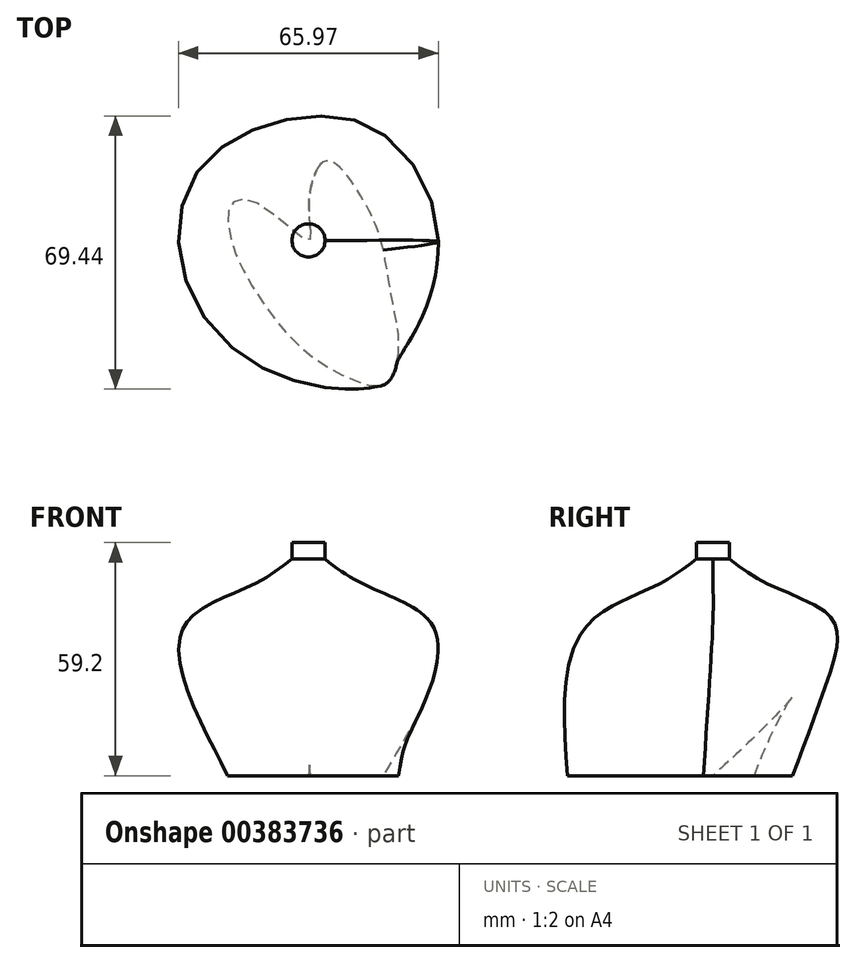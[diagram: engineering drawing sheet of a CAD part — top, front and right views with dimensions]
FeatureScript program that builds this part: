
annotation { "Feature Type Name" : "Feature", "Feature Type Description" : "" }
export const myFeature = defineFeature(function(context is Context, id is Id, definition is map)
    precondition{}
    {
        {
            var Q0;
            Q0=qCreatedBy(makeId("Top.planeOp"),FACE);
            var sketch = newSketch(context, id + "F0", { "sketchPlane" : qUnion([Q0])});
            skFitSpline(sketch, "E0", {"points": [v(0, 0) * mm, v(-12.97, 9.4) * mm, v(-19.64, 9.13) * mm, v(-19.62, 0) * mm, v(-12.36, -14.68) * mm, v(0, -28.81) * mm, v(12.9, -36.01) * mm, v(19.87, -36.29) * mm, v(22.92, -26.63) * mm, v(21.05, -14.06) * mm, v(18.37, 0) * mm, v(12.48, 12.6) * mm, v(4.5, 20.2) * mm, v(0, 8.91) * mm, v(0, 0) * mm]});
            skSolve(sketch);
        }
        {
            var Q0;
            Q0=qCreatedBy(makeId("Top.planeOp"),FACE);
            cPlane(context, id + "F1", {"entities" : qUnion([Q0]), "cplaneType" : CPlaneType.OFFSET, "offset" : 40 * mm, "width" : 152.4 * mm, "height" : 152.4 * mm});
        }
        {
            var Q0;
            Q0=qCreatedBy(id+"F1.planeOp",FACE);
            var sketch = newSketch(context, id + "F2", { "sketchPlane" : qUnion([Q0])});
            skCircle(sketch, "E1", {"center": v(0, 0) * mm, "radius": 30.1 * mm});
            skSolve(sketch);
        }
        {
            var Q0;
            Q0=qCreatedBy(makeId("Top.planeOp"),FACE);
            cPlane(context, id + "F3", {"entities" : qUnion([Q0]), "cplaneType" : CPlaneType.OFFSET, "offset" : 50 * mm, "width" : 150 * mm, "height" : 150 * mm});
        }
        {
            var Q0;
            Q0=qCreatedBy(id+"F3.planeOp",FACE);
            var sketch = newSketch(context, id + "F4", { "sketchPlane" : qUnion([Q0])});
            skCircle(sketch, "E2", {"center": v(0, 0) * mm, "radius": 11.38 * mm});
            skSolve(sketch);
        }
        {
            var Q0;
            Q0=qCreatedBy(makeId("Top.planeOp"),FACE);
            cPlane(context, id + "F5", {"entities" : qUnion([Q0]), "cplaneType" : CPlaneType.OFFSET, "offset" : 55 * mm, "width" : 150 * mm, "height" : 150 * mm});
        }
        {
            var Q0;
            Q0=qCreatedBy(id+"F5.planeOp",FACE);
            var sketch = newSketch(context, id + "F6", { "sketchPlane" : qUnion([Q0])});
            skCircle(sketch, "E3", {"center": v(0, 0) * mm, "radius": 4.2 * mm});
            skSolve(sketch);
        }
        {
            var Q0;
            Q0 = qSketchRegion(id + "F6", true);
            var Q1;
            Q1 = qSketchRegion(id + "F4", true);
            var Q2;
            Q2 = qSketchRegion(id + "F2", true);
            var Q3;
            Q3 = qSketchRegion(id + "F0", true);
            loft(context, id + "F7", {"sheetProfilesArray" : [{ "sheetProfileEntities" : qUnion([Q0]) }, { "sheetProfileEntities" : qUnion([Q1]) }, { "sheetProfileEntities" : qUnion([Q2]) }, { "sheetProfileEntities" : qUnion([Q3]) }]});
        }
        {
            var Q0;
            Q0=makeQuery(id+"F7.opLoft","CAP_FACE",FACE,{"disambiguationData":[OSD([makeQuery(id+"F6.imprint","IMPRINT",FACE,{"disambiguationData":[TD([[makeQuery(id+"F6.imprint","IMPRINT",EDGE,{"derivedFrom":sQuery(id+"F6.wireOp",EDGE,"E3")}),1.0]])]})])],"isStart":true});
            extrude(context, id + "F8", {"entities" : qUnion([Q0]), "operationType" : NewBodyOperationType.ADD, "depth" : 4.2 * mm});
        }
    });
